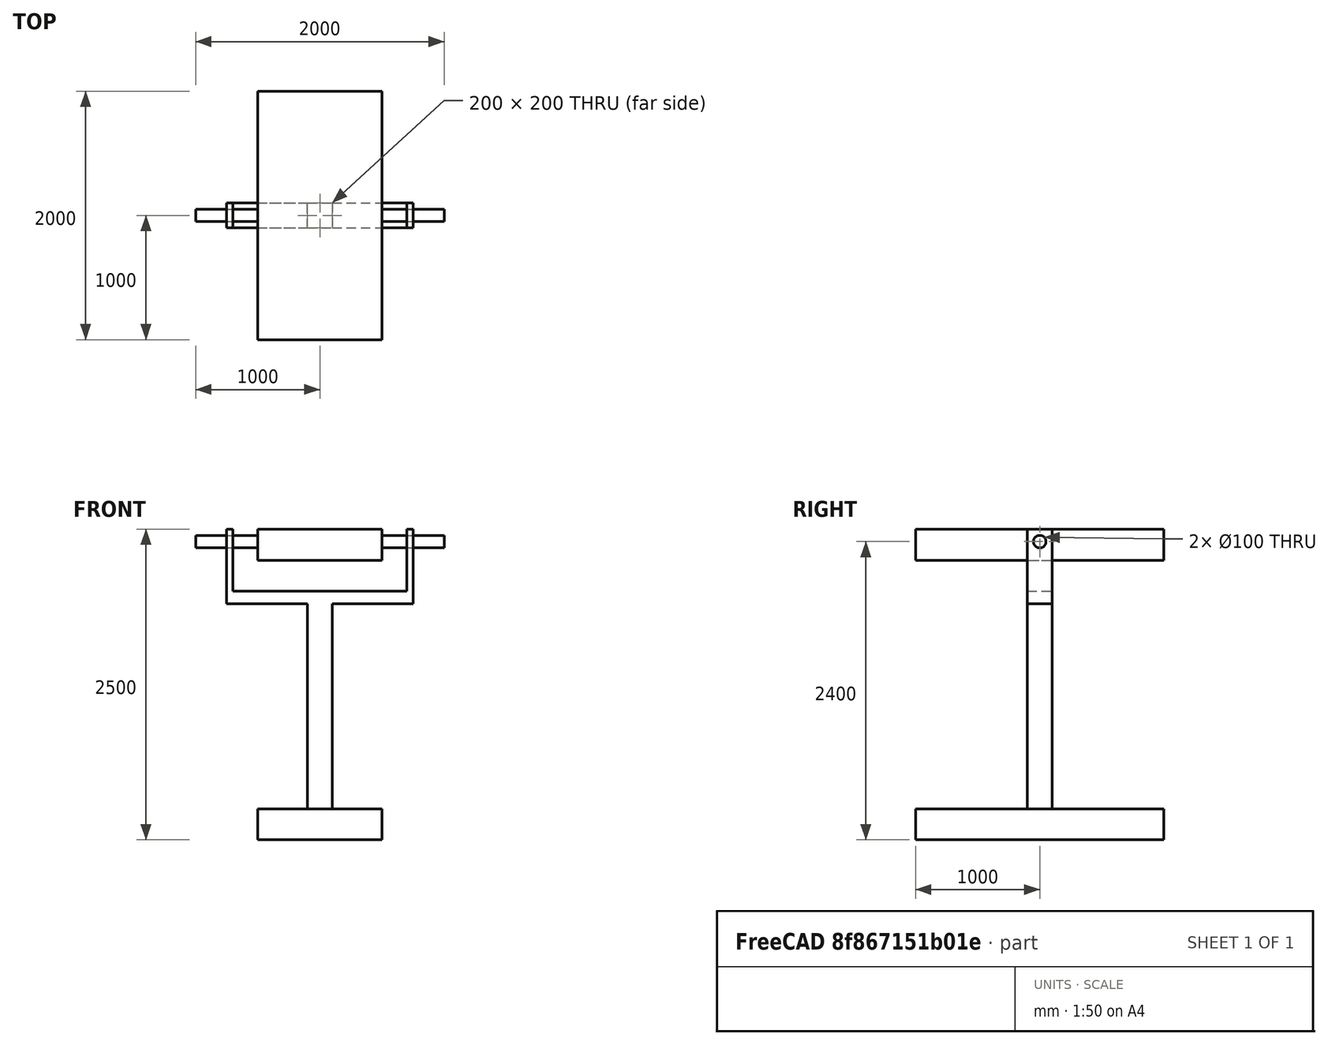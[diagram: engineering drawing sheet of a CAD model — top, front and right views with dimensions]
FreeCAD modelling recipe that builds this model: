
FCSTD DOCUMENT  (FreeCAD 0.19R24291 (Git))
Label: Balancin
License: All rights reserved
LicenseURL: http://en.wikipedia.org/wiki/All_rights_reserved
objects: Part::Box×6, Part::MultiFuse×4, Part::Cylinder×3, Part::Cut×2, App::MeasureDistance×2
note: 15 computed .brp shape members not serialized (recipe doc carries the construction recipe); baked Part::Feature solids carry a one-line shape summary decoded from their .brp

FEATURE [Part::Box] Box  label="Cubo"
  AttacherType = Attacher::AttachEngine3D
  Height = 250
  Length = 1000
  Width = 2000
FEATURE [Part::Box] Box001  label="Cubo001"
  AttacherType = Attacher::AttachEngine3D
  Height = 2000
  Length = 200
  Placement = pos=(400,900,0) rot=(0,0,1;0rad)
  Width = 200
FEATURE [Part::MultiFuse] Fusion
  Shapes = -> [Box,Box001]
FEATURE [Part::Box] Box002  label="Cubo002"
  AttacherType = Attacher::AttachEngine3D
  Height = 100
  Length = 1500
  Placement = pos=(-250,900,1900) rot=(0,0,1;0rad)
  Width = 200
FEATURE [Part::MultiFuse] Fusion001
  Shapes = -> [Fusion,Box002]
FEATURE [Part::Box] Box003  label="Cubo003"
  AttacherType = Attacher::AttachEngine3D
  Height = 500
  Length = 50
  Placement = pos=(-250,900,2000) rot=(0,0,1;0rad)
  Width = 200
FEATURE [Part::Box] Box004  label="Cubo004"
  AttacherType = Attacher::AttachEngine3D
  Height = 500
  Length = 50
  Placement = pos=(1200,900,2000) rot=(0,0,1;0rad)
  Width = 200
FEATURE [Part::MultiFuse] Fusion002
  Shapes = -> [Box004,Box003,Fusion001]
FEATURE [Part::Cylinder] Cylinder  label="Cilindro"
  Angle = 360
  AttacherType = Attacher::AttachEngine3D
  Height = 2000
  Placement = pos=(-500,1000,2400) rot=(0,1,0;1.5708rad)
  Radius = 50
FEATURE [Part::Cylinder] Cylinder001  label="Cilindro001"
  Angle = 360
  AttacherType = Attacher::AttachEngine3D
  Height = 2000
  Placement = pos=(-500,1000,2400) rot=(0,1,0;1.5708rad)
  Radius = 50
FEATURE [Part::Cylinder] Cylinder002  label="Cilindro002"
  Angle = 360
  AttacherType = Attacher::AttachEngine3D
  Height = 2000
  Placement = pos=(-500,1000,2400) rot=(0,1,0;1.5708rad)
  Radius = 50
FEATURE [Part::Cut] Cut
  Base = -> Fusion002
  Tool = -> Cylinder
FEATURE [Part::Box] Box005  label="Cubo005"
  AttacherType = Attacher::AttachEngine3D
  Height = 250
  Length = 1000
  Placement = pos=(0,0,2250) rot=(0,0,1;0rad)
  Width = 2000
FEATURE [Part::Cut] Cut001
  Base = -> Box005
  Tool = -> Cylinder001
FEATURE [Part::MultiFuse] Fusion003
  Shapes = -> [Cut001,Cylinder002]
FEATURE [App::MeasureDistance] Distance  label="Distance: 2444.64 mm"
  Distance = 2400
  P1 = (0,1000,0)
  P2 = (0,1000,2400)
FEATURE [App::MeasureDistance] Distance001  label="Distance: 995.28 mm"
  Distance = 1000
  P1 = (0,1000,0)
  P2 = (0,2000,0)
